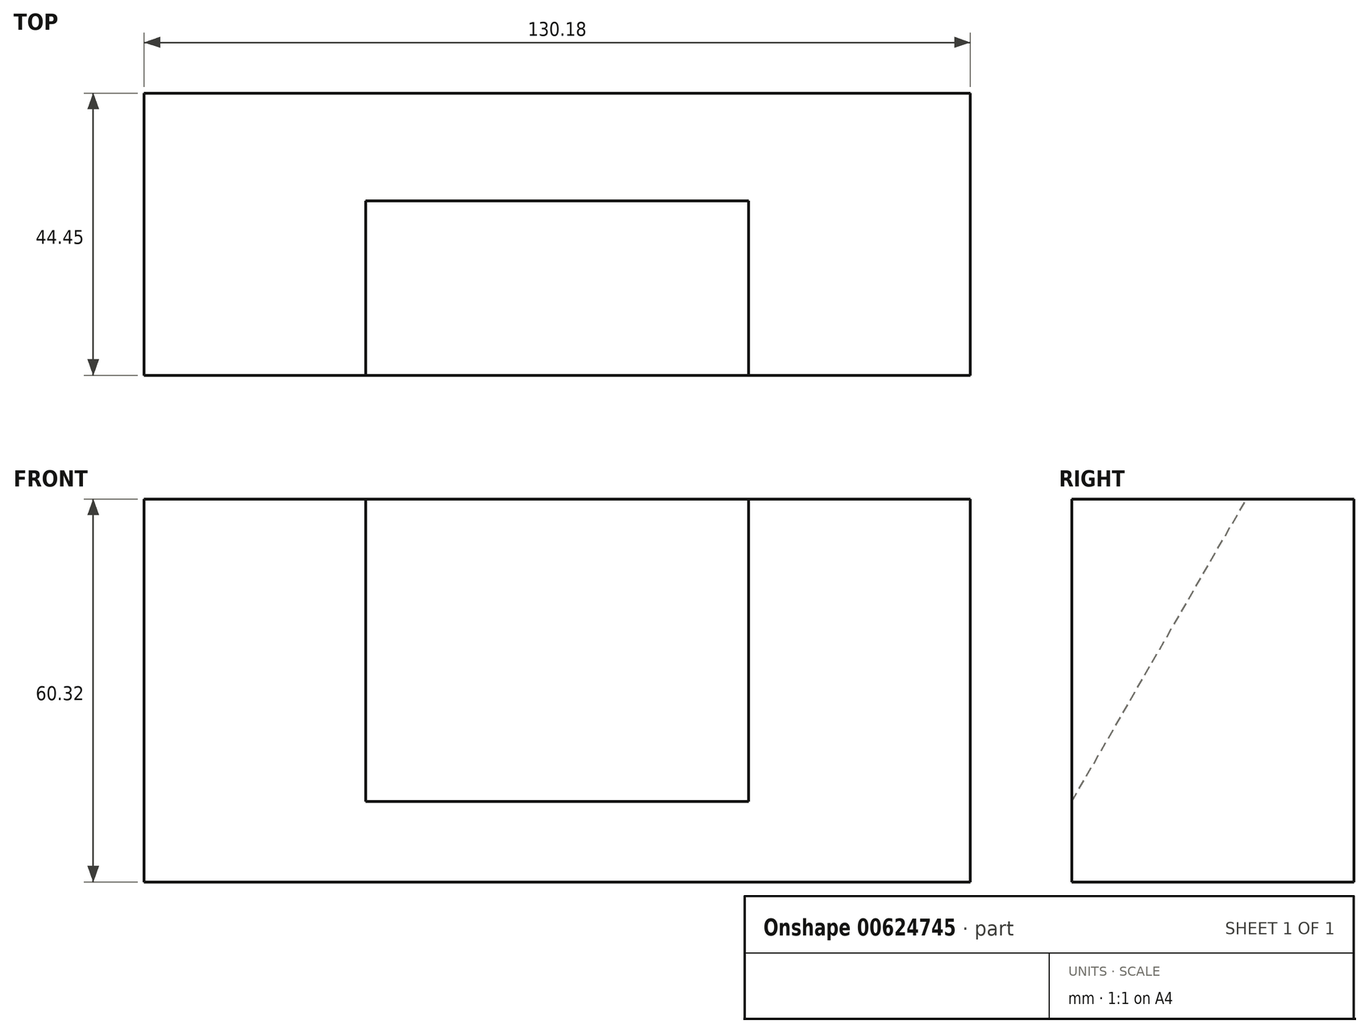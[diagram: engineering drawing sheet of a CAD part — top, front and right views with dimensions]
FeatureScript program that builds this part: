
annotation { "Feature Type Name" : "Feature", "Feature Type Description" : "" }
export const myFeature = defineFeature(function(context is Context, id is Id, definition is map)
    precondition{}
    {
        {
            var Q0;
            Q0=qCreatedBy(makeId("Front.planeOp"),FACE);
            var sketch = newSketch(context, id + "F0", { "sketchPlane" : qUnion([Q0])});
            skLineSegment(sketch, "E0.bottom", {"start": v(-65.09, 30.16) * mm, "end": v(65.09, 30.16) * mm});
            skLineSegment(sketch, "E0.top", {"start": v(-65.09, -30.16) * mm, "end": v(65.09, -30.16) * mm});
            skLineSegment(sketch, "E0.left", {"start": v(-65.09, 30.16) * mm, "end": v(-65.09, -30.16) * mm});
            skLineSegment(sketch, "E0.right", {"start": v(65.09, 30.16) * mm, "end": v(65.09, -30.16) * mm});
            skPoint(sketch, "E0.middle", {"position": v(0, 0) * mm});
            skSolve(sketch);
        }
        {
            var Q0;
            Q0=makeQuery(id+"F0.imprint","IMPRINT",FACE,{"disambiguationData":[TD([[makeQuery(id+"F0.imprint","IMPRINT",EDGE,{"derivedFrom":sQuery(id+"F0.wireOp",EDGE,"E0.bottom")}),-1.0]])]});
            extrude(context, id + "F1", {"entities" : qUnion([Q0]), "depth" : 44.45 * mm, "offsetDistance" : 25.4 * mm});
        }
        {
            var Q0;
            Q0=qCreatedBy(makeId("Right.planeOp"),FACE);
            var sketch = newSketch(context, id + "F2", { "sketchPlane" : qUnion([Q0])});
            skLineSegment(sketch, "E1", {"start": v(-44.45, 30.16) * mm, "end": v(-44.45, -17.46) * mm});
            skLineSegment(sketch, "E2", {"start": v(-44.45, -17.46) * mm, "end": v(-16.95, 30.16) * mm});
            skLineSegment(sketch, "E3", {"start": v(-44.45, 30.16) * mm, "end": v(-16.95, 30.16) * mm});
            skSolve(sketch);
        }
        {
            var Q0;
            Q0 = qSketchRegion(id + "F2", true);
            extrude(context, id + "F3", {"entities" : qUnion([Q0]), "operationType" : NewBodyOperationType.REMOVE, "endBound" : BoundingType.SYMMETRIC, "depth" : 60.32 * mm, "offsetDistance" : 25.4 * mm});
        }
    });
